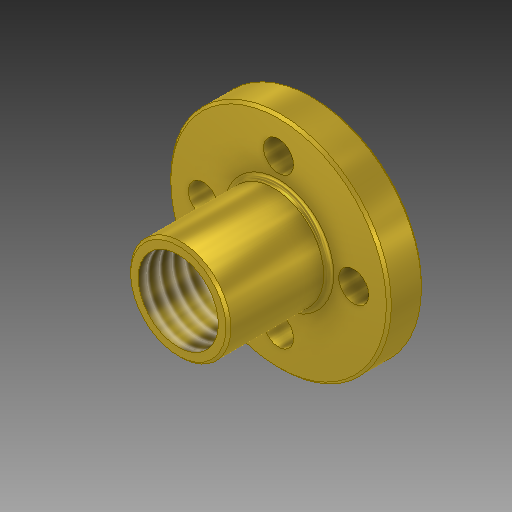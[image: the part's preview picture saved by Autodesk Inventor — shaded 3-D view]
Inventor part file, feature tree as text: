
AUTODESK INVENTOR PART (.ipt)
format: ipt  version: 2019 (Build 230136000, 136)  size: 208,384 bytes
history: native  units: mm
features: extrude x5, sketch x5, chamfer x2, fillet x1, thread x1
ambient origin geometry x8: Origin, YZ Plane, XZ Plane, XY Plane, X Axis, Y Axis, Z Axis, Center Point
bodies: Solid1 (feature_tree)
feature tree (14):
  extrude  "Extrusion1"  Depth=3.5mm TaperAngle=0.0deg
  extrude  "Extrusion2"  Depth=10.0mm
  extrude  "Extrusion3"  Depth=10.0mm
  extrude  "Extrusion4"  Depth=10.0mm
  fillet  "Fillet1"  Radius=2.0mm
  chamfer  "Chamfer1"  Distance=2.0mm Angle=45.0deg
  chamfer  "Chamfer2"  Distance=2.0mm Angle=45.0deg
  extrude  "Extrusion5"  Depth=10.0mm
  thread  "Thread1"  [1 undecoded]
  sketch  "Sketch1"  dims[d0=22.0mm d1=3.5mm d2=0.0mm]
  sketch  "Sketch2"  dims[d3=10.0mm d4=8.0mm]
  sketch  "Sketch3"  dims[d5=10.0mm d6=0.0mm d7=8.0mm]
  sketch  "Sketch4"  dims[d8=10.0mm d9=0.0mm d10=10.0mm d11=2.0mm d12=0.0mm]
  sketch  "Sketch5"  dims[d13=0.5mm d14=0.25mm d15=2.0mm d16=45.0deg d17=0.25mm d18=2.0mm d19=45.0deg d20=22.0mm d21=15.0mm d22=3.0mm d23=40.0mm d25=360.0deg d27=2.0mm d28=0.0mm d29=10.0mm d30=0.0mm]
note: 1 required parameter value undecoded (feature->parameter linkage not recoverable at this tier; creation-order binding heuristic only, values carry confidence <= 0.55)
